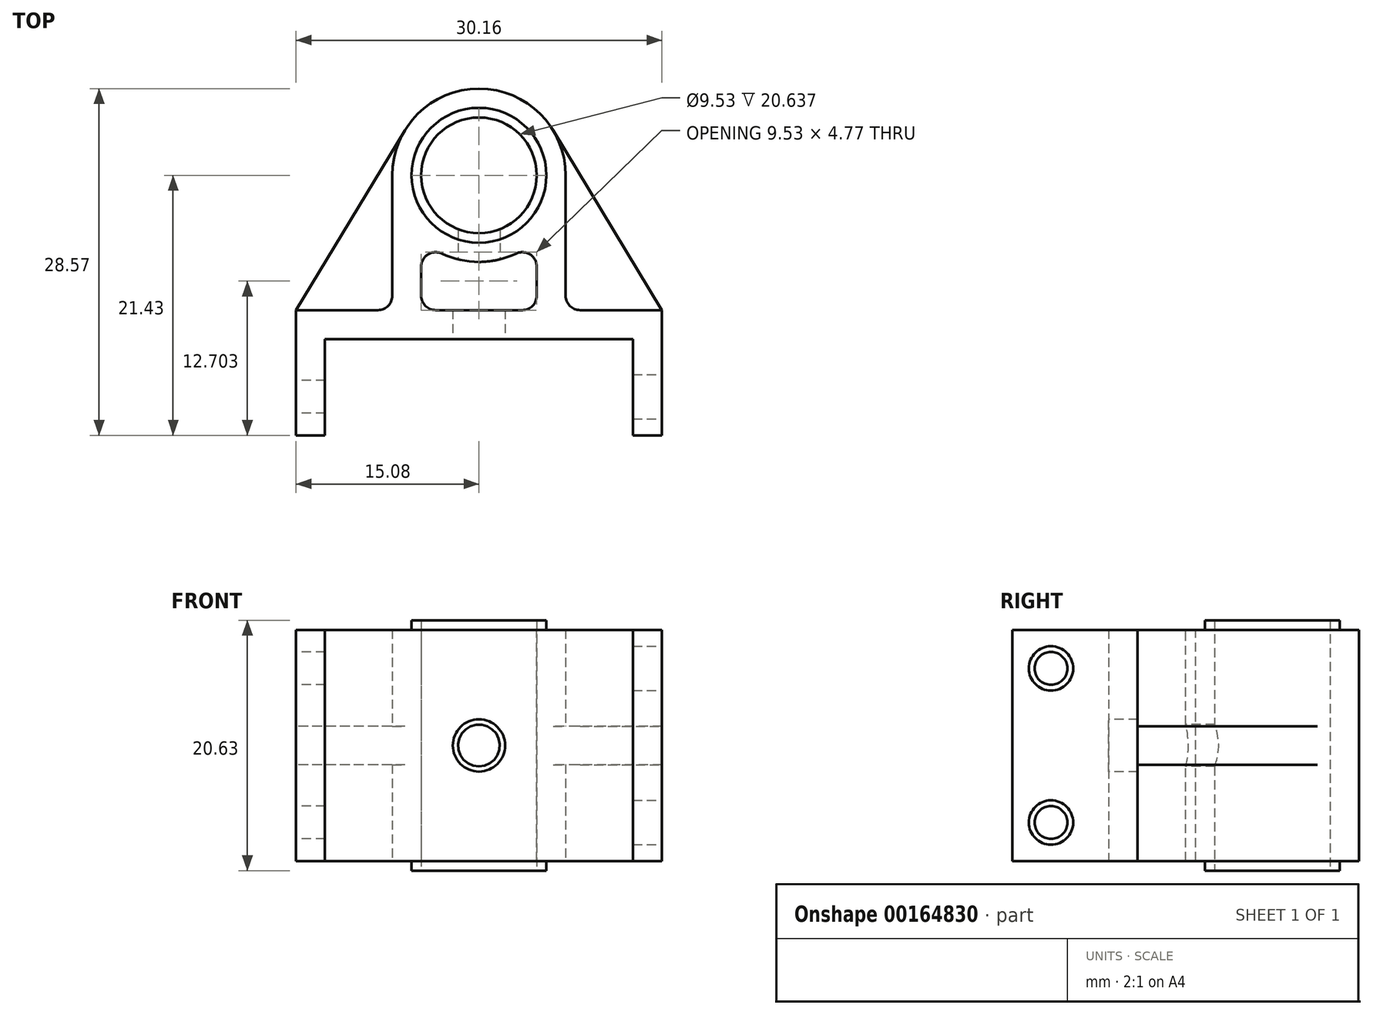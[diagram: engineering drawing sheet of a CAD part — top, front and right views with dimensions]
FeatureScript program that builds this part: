
annotation { "Feature Type Name" : "Feature", "Feature Type Description" : "" }
export const myFeature = defineFeature(function(context is Context, id is Id, definition is map)
    precondition{}
    {
        {
            var Q0;
            Q0=qCreatedBy(makeId("Top.planeOp"),FACE);
            var sketch = newSketch(context, id + "F0", { "sketchPlane" : qUnion([Q0])});
            skArc(sketch, "E0", {"start": v(7.14, 0) * mm, "mid": v(0, 7.14) * mm, "end": v(-7.14, 0) * mm});
            skCircle(sketch, "E1", {"center": v(0, 0) * mm, "radius": 4.76 * mm});
            skLineSegment(sketch, "E2.bottom", {"start": v(12.7, -21.43) * mm, "end": v(-12.7, -21.43) * mm, "construction": true});
            skLineSegment(sketch, "E2.top", {"start": v(12.7, -13.5) * mm, "end": v(-12.7, -13.5) * mm});
            skLineSegment(sketch, "E2.left", {"start": v(12.7, -21.43) * mm, "end": v(12.7, -13.5) * mm});
            skLineSegment(sketch, "E2.right", {"start": v(-12.7, -21.43) * mm, "end": v(-12.7, -13.5) * mm});
            skLineSegment(sketch, "E3", {"start": v(12.7, -21.43) * mm, "end": v(15.08, -21.43) * mm});
            skLineSegment(sketch, "E4", {"start": v(-12.7, -21.43) * mm, "end": v(-15.08, -21.43) * mm});
            skLineSegment(sketch, "E5", {"start": v(-15.08, -21.43) * mm, "end": v(-15.08, -11.11) * mm});
            skLineSegment(sketch, "E6", {"start": v(15.08, -21.43) * mm, "end": v(15.08, -11.11) * mm});
            skLineSegment(sketch, "E7", {"start": v(-15.08, -11.11) * mm, "end": v(-7.14, -11.11) * mm});
            skLineSegment(sketch, "E8", {"start": v(-7.14, -11.11) * mm, "end": v(-7.14, 0) * mm});
            skLineSegment(sketch, "E9", {"start": v(15.08, -11.11) * mm, "end": v(7.14, -11.11) * mm});
            skLineSegment(sketch, "E10", {"start": v(7.14, -11.11) * mm, "end": v(7.14, 0) * mm});
            skLineSegment(sketch, "E11", {"start": v(-7.14, 0) * mm, "end": v(7.14, 0) * mm, "construction": true});
            skLineSegment(sketch, "E12", {"start": v(-7.14, -11.11) * mm, "end": v(7.14, -11.11) * mm, "construction": true});
            skLineSegment(sketch, "E13", {"start": v(0, -11.11) * mm, "end": v(0, -13.5) * mm, "construction": true});
            skSolve(sketch);
        }
        {
            var Q0;
            Q0=qSketchRegion(id+"F0",true);
            extrude(context, id + "F1", {"entities" : qUnion([Q0]), "depth" : 19.05 * mm});
        }
        {
            var Q0;
            Q0=makeQuery(id+"F1.opExtrude","SWEPT_FACE",FACE,{"disambiguationData":[OSD([sQuery(id+"F0.wireOp",EDGE,"E6")])]});
            var sketch = newSketch(context, id + "F2", { "sketchPlane" : qUnion([Q0])});
            skLineSegment(sketch, "E14.bottom", {"start": v(-21.43, 19.05) * mm, "end": v(-18.26, 19.05) * mm, "construction": true});
            skLineSegment(sketch, "E14.top", {"start": v(-21.43, 15.88) * mm, "end": v(-18.26, 15.88) * mm, "construction": true});
            skLineSegment(sketch, "E14.left", {"start": v(-21.43, 19.05) * mm, "end": v(-21.43, 15.88) * mm, "construction": true});
            skLineSegment(sketch, "E14.right", {"start": v(-18.26, 19.05) * mm, "end": v(-18.26, 15.88) * mm, "construction": true});
            skLineSegment(sketch, "E15.bottom", {"start": v(-21.43, 0) * mm, "end": v(-18.26, 0) * mm, "construction": true});
            skLineSegment(sketch, "E15.top", {"start": v(-21.43, 3.18) * mm, "end": v(-18.26, 3.18) * mm, "construction": true});
            skLineSegment(sketch, "E15.left", {"start": v(-21.43, 0) * mm, "end": v(-21.43, 3.18) * mm, "construction": true});
            skLineSegment(sketch, "E15.right", {"start": v(-18.26, 0) * mm, "end": v(-18.26, 3.18) * mm, "construction": true});
            skCircle(sketch, "E16", {"center": v(-18.26, 15.88) * mm, "radius": 1.83 * mm});
            skCircle(sketch, "E17", {"center": v(-18.26, 3.18) * mm, "radius": 1.83 * mm});
            skSolve(sketch);
        }
        {
            var Q0;
            Q0=qSketchRegion(id+"F2",true);
            var Q1;
            Q1=makeQuery(id+"F1.opExtrude","SWEPT_FACE",FACE,{"disambiguationData":[OSD([sQuery(id+"F0.wireOp",EDGE,"E2.left")])]});
            extrude(context, id + "F3", {"entities" : qUnion([Q0]), "operationType" : NewBodyOperationType.REMOVE, "endBound" : BoundingType.UP_TO_SURFACE, "oppositeDirection" : true, "endBoundEntityFace" : qUnion([Q1]), "depth" : 25.4 * mm});
        }
        {
            var Q0;
            Q0=makeQuery(id+"F1.opExtrude","SWEPT_FACE",FACE,{"disambiguationData":[OSD([sQuery(id+"F0.wireOp",EDGE,"E5")])]});
            var sketch = newSketch(context, id + "F4", { "sketchPlane" : qUnion([Q0])});
            skCircle(sketch, "E18", {"center": v(18.26, 3.18) * mm, "radius": 1.35 * mm});
            skCircle(sketch, "E19", {"center": v(18.26, 15.88) * mm, "radius": 1.35 * mm});
            skSolve(sketch);
        }
        {
            var Q0;
            Q0=qSketchRegion(id+"F4",true);
            var Q1;
            Q1=makeQuery(id+"F1.opExtrude","SWEPT_FACE",FACE,{"disambiguationData":[OSD([sQuery(id+"F0.wireOp",EDGE,"E2.right")])]});
            extrude(context, id + "F5", {"entities" : qUnion([Q0]), "operationType" : NewBodyOperationType.REMOVE, "endBound" : BoundingType.UP_TO_SURFACE, "oppositeDirection" : true, "endBoundEntityFace" : qUnion([Q1]), "depth" : 25.4 * mm});
        }
        {
            var Q0;
            Q0=makeQuery(id+"F1.opExtrude","CAP_FACE",FACE,{"disambiguationData":[OSD([sQuery(id+"F0.wireOp",EDGE,"E0"),sQuery(id+"F0.wireOp",EDGE,"E1"),sQuery(id+"F0.wireOp",EDGE,"E2.top"),sQuery(id+"F0.wireOp",EDGE,"E2.left"),sQuery(id+"F0.wireOp",EDGE,"E2.right"),sQuery(id+"F0.wireOp",EDGE,"E3"),sQuery(id+"F0.wireOp",EDGE,"E4"),sQuery(id+"F0.wireOp",EDGE,"E5"),sQuery(id+"F0.wireOp",EDGE,"E6"),sQuery(id+"F0.wireOp",EDGE,"E7"),sQuery(id+"F0.wireOp",EDGE,"E8"),sQuery(id+"F0.wireOp",EDGE,"E9"),sQuery(id+"F0.wireOp",EDGE,"E10")])],"isStart":true});
            cPlane(context, id + "F6", {"entities" : qUnion([Q0]), "cplaneType" : CPlaneType.OFFSET, "offset" : 9.52 * mm, "oppositeDirection" : true, "width" : 152.4 * mm, "height" : 152.4 * mm});
        }
        {
            var Q0;
            Q0=qCreatedBy(id+"F6.planeOp",FACE);
            var sketch = newSketch(context, id + "F7", { "sketchPlane" : qUnion([Q0])});
            skLineSegment(sketch, "E20", {"start": v(-6.11, -3.7) * mm, "end": v(-15.08, 11.11) * mm});
            skArc(sketch, "E21", {"start": v(-7.14, 0) * mm, "mid": v(-6.88, -1.92) * mm, "end": v(-6.11, -3.7) * mm});
            skLineSegment(sketch, "E22", {"start": v(-7.14, 0) * mm, "end": v(-7.14, 11.11) * mm});
            skLineSegment(sketch, "E23", {"start": v(-7.14, 11.11) * mm, "end": v(-15.08, 11.11) * mm});
            skArc(sketch, "E24", {"start": v(6.11, -3.7) * mm, "mid": v(6.88, -1.92) * mm, "end": v(7.14, 0) * mm});
            skLineSegment(sketch, "E25", {"start": v(7.14, 0) * mm, "end": v(7.14, 11.11) * mm});
            skLineSegment(sketch, "E26", {"start": v(7.14, 11.11) * mm, "end": v(15.08, 11.11) * mm});
            skLineSegment(sketch, "E27", {"start": v(15.08, 11.11) * mm, "end": v(6.11, -3.7) * mm});
            skSolve(sketch);
        }
        {
            var Q0;
            Q0 = qSketchRegion(id + "F7", true);
            extrude(context, id + "F8", {"entities" : qUnion([Q0]), "operationType" : NewBodyOperationType.ADD, "endBound" : BoundingType.SYMMETRIC, "depth" : 3.17 * mm});
        }
        {
            var Q0;
            Q0=makeQuery(id+"F1.opExtrude","CAP_FACE",FACE,{"disambiguationData":[OSD([sQuery(id+"F0.wireOp",EDGE,"E0"),sQuery(id+"F0.wireOp",EDGE,"E1"),sQuery(id+"F0.wireOp",EDGE,"E2.top"),sQuery(id+"F0.wireOp",EDGE,"E2.left"),sQuery(id+"F0.wireOp",EDGE,"E2.right"),sQuery(id+"F0.wireOp",EDGE,"E3"),sQuery(id+"F0.wireOp",EDGE,"E4"),sQuery(id+"F0.wireOp",EDGE,"E5"),sQuery(id+"F0.wireOp",EDGE,"E6"),sQuery(id+"F0.wireOp",EDGE,"E7"),sQuery(id+"F0.wireOp",EDGE,"E8"),sQuery(id+"F0.wireOp",EDGE,"E9"),sQuery(id+"F0.wireOp",EDGE,"E10")])],"isStart":true});
            var sketch = newSketch(context, id + "F9", { "sketchPlane" : qUnion([Q0])});
            skCircle(sketch, "E28", {"center": v(0, 0) * mm, "radius": 4.76 * mm});
            skCircle(sketch, "E29", {"center": v(0, 0) * mm, "radius": 5.56 * mm});
            skSolve(sketch);
        }
        {
            var Q0;
            Q0=makeQuery(id+"F1.opExtrude","CAP_FACE",FACE,{"disambiguationData":[OSD([sQuery(id+"F0.wireOp",EDGE,"E0"),sQuery(id+"F0.wireOp",EDGE,"E1"),sQuery(id+"F0.wireOp",EDGE,"E2.top"),sQuery(id+"F0.wireOp",EDGE,"E2.left"),sQuery(id+"F0.wireOp",EDGE,"E2.right"),sQuery(id+"F0.wireOp",EDGE,"E3"),sQuery(id+"F0.wireOp",EDGE,"E4"),sQuery(id+"F0.wireOp",EDGE,"E5"),sQuery(id+"F0.wireOp",EDGE,"E6"),sQuery(id+"F0.wireOp",EDGE,"E7"),sQuery(id+"F0.wireOp",EDGE,"E8"),sQuery(id+"F0.wireOp",EDGE,"E9"),sQuery(id+"F0.wireOp",EDGE,"E10")])],"isStart":false});
            cPlane(context, id + "F10", {"entities" : qUnion([Q0]), "cplaneType" : CPlaneType.OFFSET, "offset" : 0.8 * mm, "width" : 152.4 * mm, "height" : 152.4 * mm});
        }
        {
            var Q0;
            Q0 = qSketchRegion(id + "F9", true);
            var Q1;
            Q1=qCreatedBy(id+"F10.planeOp",FACE);
            extrude(context, id + "F11", {"entities" : qUnion([Q0]), "operationType" : NewBodyOperationType.ADD, "depth" : 0.8 * mm, "hasSecondDirection" : true, "secondDirectionBound" : SecondDirectionBoundingType.UP_TO_SURFACE, "secondDirectionOppositeDirection" : true, "secondDirectionBoundEntityFace" : qUnion([Q1]), "secondDirectionDepth" : 25.4 * mm});
        }
        {
            var Q0;
            Q0=makeQuery(id+"F1.opExtrude","SWEPT_FACE",FACE,{"disambiguationData":[OSD([sQuery(id+"F0.wireOp",EDGE,"E2.top")])]});
            var sketch = newSketch(context, id + "F12", { "sketchPlane" : qUnion([Q0])});
            skLineSegment(sketch, "E30", {"start": v(0, 19.05) * mm, "end": v(0, 0) * mm, "construction": true});
            skCircle(sketch, "E31", {"center": v(0, 9.53) * mm, "radius": 1.73 * mm});
            skSolve(sketch);
        }
        {
            var Q0;
            Q0 = qSketchRegion(id + "F12", true);
            var Q1;
            Q1=makeQuery(id+"F11.boolean.opBoolean","MERGE",FACE,{"derivedFrom":[makeQuery(id+"F1.opExtrude","SWEPT_FACE",FACE,{"disambiguationData":[OSD([sQuery(id+"F0.wireOp",EDGE,"E1")])]}),makeQuery(id+"F11.opExtrude","SWEPT_FACE",FACE,{"disambiguationData":[OSD([sQuery(id+"F9.wireOp",EDGE,"E28")])]})]});
            extrude(context, id + "F13", {"entities" : qUnion([Q0]), "operationType" : NewBodyOperationType.REMOVE, "endBound" : BoundingType.UP_TO_SURFACE, "oppositeDirection" : true, "endBoundEntityFace" : qUnion([Q1]), "depth" : 25.4 * mm});
        }
        {
            var Q0;
            Q0=makeQuery(id+"F1.opExtrude","CAP_FACE",FACE,{"disambiguationData":[OSD([sQuery(id+"F0.wireOp",EDGE,"E0"),sQuery(id+"F0.wireOp",EDGE,"E1"),sQuery(id+"F0.wireOp",EDGE,"E2.top"),sQuery(id+"F0.wireOp",EDGE,"E2.left"),sQuery(id+"F0.wireOp",EDGE,"E2.right"),sQuery(id+"F0.wireOp",EDGE,"E3"),sQuery(id+"F0.wireOp",EDGE,"E4"),sQuery(id+"F0.wireOp",EDGE,"E5"),sQuery(id+"F0.wireOp",EDGE,"E6"),sQuery(id+"F0.wireOp",EDGE,"E7"),sQuery(id+"F0.wireOp",EDGE,"E8"),sQuery(id+"F0.wireOp",EDGE,"E9"),sQuery(id+"F0.wireOp",EDGE,"E10")])],"isStart":false});
            var sketch = newSketch(context, id + "F14", { "sketchPlane" : qUnion([Q0])});
            skLineSegment(sketch, "E32.bottom", {"start": v(-4.76, -11.11) * mm, "end": v(4.76, -11.11) * mm});
            skLineSegment(sketch, "E32.top", {"start": v(-4.76, -5.32) * mm, "end": v(4.76, -5.32) * mm, "construction": true});
            skLineSegment(sketch, "E32.left", {"start": v(-4.76, -11.11) * mm, "end": v(-4.76, -5.32) * mm});
            skLineSegment(sketch, "E32.right", {"start": v(4.76, -11.11) * mm, "end": v(4.76, -5.32) * mm});
            skLineSegment(sketch, "E33", {"start": v(0, -11.11) * mm, "end": v(0, -13.5) * mm, "construction": true});
            skLineSegment(sketch, "E34", {"start": v(4.76, -11.11) * mm, "end": v(7.14, -11.11) * mm, "construction": true});
            skArc(sketch, "E35", {"start": v(-4.76, -5.32) * mm, "mid": v(0, -7.14) * mm, "end": v(4.76, -5.32) * mm});
            skSolve(sketch);
        }
        {
            var Q0;
            Q0 = qSketchRegion(id + "F14", true);
            var Q1;
            Q1=makeQuery(id+"F1.opExtrude","CAP_FACE",FACE,{"disambiguationData":[OSD([sQuery(id+"F0.wireOp",EDGE,"E0"),sQuery(id+"F0.wireOp",EDGE,"E1"),sQuery(id+"F0.wireOp",EDGE,"E2.top"),sQuery(id+"F0.wireOp",EDGE,"E2.left"),sQuery(id+"F0.wireOp",EDGE,"E2.right"),sQuery(id+"F0.wireOp",EDGE,"E3"),sQuery(id+"F0.wireOp",EDGE,"E4"),sQuery(id+"F0.wireOp",EDGE,"E5"),sQuery(id+"F0.wireOp",EDGE,"E6"),sQuery(id+"F0.wireOp",EDGE,"E7"),sQuery(id+"F0.wireOp",EDGE,"E8"),sQuery(id+"F0.wireOp",EDGE,"E9"),sQuery(id+"F0.wireOp",EDGE,"E10")])],"isStart":true});
            extrude(context, id + "F15", {"entities" : qUnion([Q0]), "operationType" : NewBodyOperationType.REMOVE, "endBound" : BoundingType.UP_TO_SURFACE, "oppositeDirection" : true, "endBoundEntityFace" : qUnion([Q1]), "depth" : 25.4 * mm});
        }
        {
            var Q0;
            Q0=makeQuery(id+"F1.opExtrude","SWEPT_FACE",FACE,{"disambiguationData":[OSD([sQuery(id+"F0.wireOp",EDGE,"E2.top")])]});
            var sketch = newSketch(context, id + "F16", { "sketchPlane" : qUnion([Q0])});
            skCircle(sketch, "E36", {"center": v(0, 9.53) * mm, "radius": 2.15 * mm});
            skSolve(sketch);
        }
        {
            var Q0;
            Q0 = qSketchRegion(id + "F16", true);
            var Q1;
            Q1=makeQuery(id+"F15.boolean.opBoolean","COPY",FACE,{"derivedFrom":makeQuery(id+"F15.opExtrude","SWEPT_FACE",FACE,{"disambiguationData":[OSD([sQuery(id+"F14.wireOp",EDGE,"E32.bottom")])]})});
            extrude(context, id + "F17", {"entities" : qUnion([Q0]), "operationType" : NewBodyOperationType.REMOVE, "endBound" : BoundingType.UP_TO_SURFACE, "oppositeDirection" : true, "endBoundEntityFace" : qUnion([Q1]), "depth" : 25.4 * mm});
        }
        {
            var Q0;
            {var subQ0=sQuery(id+"F0.wireOp",EDGE,"E10");var subQ1=sQuery(id+"F0.wireOp",EDGE,"E9");Q0=makeQuery(id+"F8.boolean.opBoolean","SPLIT",EDGE,{"disambiguationData":[TD([makeQuery(id+"F8.opExtrude","CAP_FACE",FACE,{"disambiguationData":[OSD([sQuery(id+"F7.wireOp",EDGE,"E24"),sQuery(id+"F7.wireOp",EDGE,"E25"),sQuery(id+"F7.wireOp",EDGE,"E26"),sQuery(id+"F7.wireOp",EDGE,"E27")])],"isStart":true})])],"derivedFrom":makeQuery(id+"F1.opExtrude","SWEPT_EDGE",EDGE,{"disambiguationData":[OSD([subQ1,subQ0])]})});}
            var Q1;
            {var subQ0=sQuery(id+"F0.wireOp",EDGE,"E10");var subQ1=sQuery(id+"F0.wireOp",EDGE,"E9");Q1=makeQuery(id+"F8.boolean.opBoolean","SPLIT",EDGE,{"disambiguationData":[TD([makeQuery(id+"F8.opExtrude","CAP_FACE",FACE,{"disambiguationData":[OSD([sQuery(id+"F7.wireOp",EDGE,"E24"),sQuery(id+"F7.wireOp",EDGE,"E25"),sQuery(id+"F7.wireOp",EDGE,"E26"),sQuery(id+"F7.wireOp",EDGE,"E27")])],"isStart":false})])],"derivedFrom":makeQuery(id+"F1.opExtrude","SWEPT_EDGE",EDGE,{"disambiguationData":[OSD([subQ1,subQ0])]})});}
            var Q2;
            {var subQ0=sQuery(id+"F0.wireOp",EDGE,"E8");var subQ1=sQuery(id+"F0.wireOp",EDGE,"E7");Q2=makeQuery(id+"F8.boolean.opBoolean","SPLIT",EDGE,{"disambiguationData":[TD([makeQuery(id+"F8.opExtrude","CAP_FACE",FACE,{"disambiguationData":[OSD([sQuery(id+"F7.wireOp",EDGE,"E20"),sQuery(id+"F7.wireOp",EDGE,"E21"),sQuery(id+"F7.wireOp",EDGE,"E22"),sQuery(id+"F7.wireOp",EDGE,"E23")])],"isStart":true})])],"derivedFrom":makeQuery(id+"F1.opExtrude","SWEPT_EDGE",EDGE,{"disambiguationData":[OSD([subQ1,subQ0])]})});}
            var Q3;
            {var subQ0=sQuery(id+"F0.wireOp",EDGE,"E8");var subQ1=sQuery(id+"F0.wireOp",EDGE,"E7");Q3=makeQuery(id+"F8.boolean.opBoolean","SPLIT",EDGE,{"disambiguationData":[TD([makeQuery(id+"F8.opExtrude","CAP_FACE",FACE,{"disambiguationData":[OSD([sQuery(id+"F7.wireOp",EDGE,"E20"),sQuery(id+"F7.wireOp",EDGE,"E21"),sQuery(id+"F7.wireOp",EDGE,"E22"),sQuery(id+"F7.wireOp",EDGE,"E23")])],"isStart":false})])],"derivedFrom":makeQuery(id+"F1.opExtrude","SWEPT_EDGE",EDGE,{"disambiguationData":[OSD([subQ1,subQ0])]})});}
            var Q4;
            Q4=makeQuery(id+"F15.boolean.opBoolean","COPY",EDGE,{"derivedFrom":makeQuery(id+"F15.opExtrude","SWEPT_EDGE",EDGE,{"disambiguationData":[OSD([sQuery(id+"F14.wireOp",EDGE,"E32.bottom"),sQuery(id+"F14.wireOp",EDGE,"E32.left")])]})});
            var Q5;
            Q5=makeQuery(id+"F15.boolean.opBoolean","COPY",EDGE,{"derivedFrom":makeQuery(id+"F15.opExtrude","SWEPT_EDGE",EDGE,{"disambiguationData":[OSD([sQuery(id+"F14.wireOp",EDGE,"E32.bottom"),sQuery(id+"F14.wireOp",EDGE,"E32.right")])]})});
            var Q6;
            Q6=makeQuery(id+"F15.boolean.opBoolean","COPY",EDGE,{"derivedFrom":makeQuery(id+"F15.opExtrude","SWEPT_EDGE",EDGE,{"disambiguationData":[OSD([sQuery(id+"F14.wireOp",EDGE,"E32.right"),sQuery(id+"F14.wireOp",EDGE,"E35")])]})});
            var Q7;
            Q7=makeQuery(id+"F15.boolean.opBoolean","COPY",EDGE,{"derivedFrom":makeQuery(id+"F15.opExtrude","SWEPT_EDGE",EDGE,{"disambiguationData":[OSD([sQuery(id+"F14.wireOp",EDGE,"E32.left"),sQuery(id+"F14.wireOp",EDGE,"E35")])]})});
            fillet(context, id + "F18", {"entities" : qUnion([Q0, Q1, Q2, Q3, Q4, Q5, Q6, Q7]), "radius" : 1.2 * mm, "tangentPropagation" : true, "allowEdgeOverflow" : false});
        }
    });
